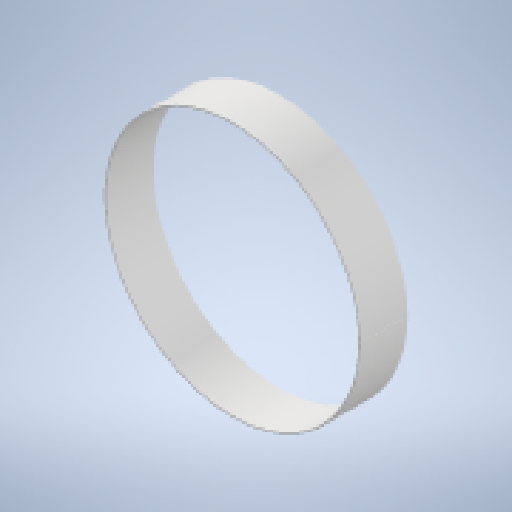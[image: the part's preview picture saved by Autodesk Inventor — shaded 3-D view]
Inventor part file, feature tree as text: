
AUTODESK INVENTOR PART (.ipt)
format: ipt  version: 2025 (Build 290162010, 162A)  size: 278,528 bytes
history: native  units: mm
features: revolve x1, sketch x1, other x1
ambient origin geometry x8: Origin, YZ Plane, XZ Plane, XY Plane, X Axis, Y Axis, Z Axis, Center Point
bodies: Solid1 (feature_tree)
feature tree (3):
  revolve  "Revolution1"  [1 undecoded]
  sketch  "Sketch3"  dims[d1=3.0mm d2=100.0mm d3=270.0mm d4=62.8144mm]
  other  "Definition1"
note: 1 required parameter value undecoded (feature->parameter linkage not recoverable at this tier; creation-order binding heuristic only, values carry confidence <= 0.55)
